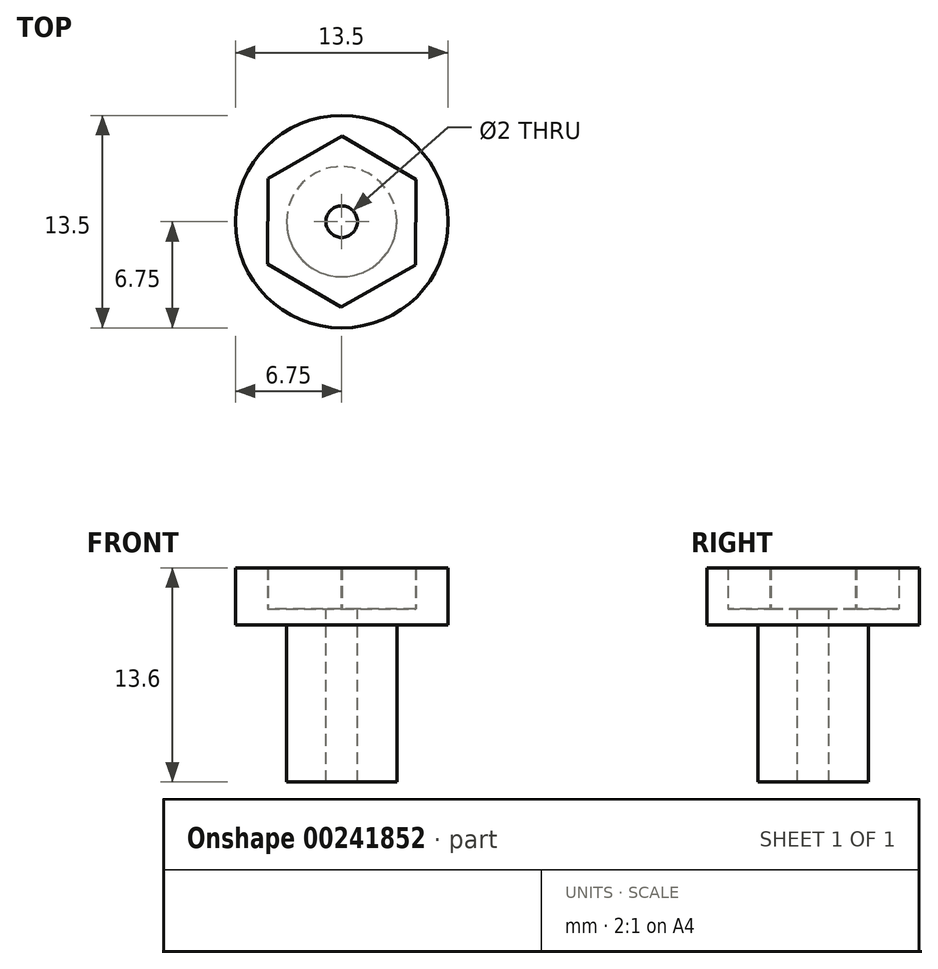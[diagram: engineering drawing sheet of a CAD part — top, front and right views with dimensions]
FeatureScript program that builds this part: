
annotation { "Feature Type Name" : "Feature", "Feature Type Description" : "" }
export const myFeature = defineFeature(function(context is Context, id is Id, definition is map)
    precondition{}
    {
        {
            var Q0;
            Q0=qCreatedBy(makeId("Top.planeOp"),FACE);
            var sketch = newSketch(context, id + "F0", { "sketchPlane" : qUnion([Q0])});
            skCircle(sketch, "E0", {"center": v(0, 0) * mm, "radius": 6.75 * mm});
            skCircle(sketch, "E1.cCircle", {"center": v(0, 0) * mm, "radius": 4.7 * mm, "construction": true});
            skLineSegment(sketch, "E1.0", {"start": v(0.04, 5.43) * mm, "end": v(4.72, 2.68) * mm});
            skLineSegment(sketch, "E1.1", {"start": v(4.72, 2.68) * mm, "end": v(4.68, -2.75) * mm});
            skLineSegment(sketch, "E1.2", {"start": v(4.68, -2.75) * mm, "end": v(-0.04, -5.43) * mm});
            skLineSegment(sketch, "E1.3", {"start": v(-0.04, -5.43) * mm, "end": v(-4.72, -2.68) * mm});
            skLineSegment(sketch, "E1.4", {"start": v(-4.72, -2.68) * mm, "end": v(-4.68, 2.75) * mm});
            skLineSegment(sketch, "E1.5", {"start": v(-4.68, 2.75) * mm, "end": v(0.04, 5.43) * mm});
            skPoint(sketch, "E1.0.midPoint", {"position": v(2.38, 4.05) * mm});
            skSolve(sketch);
        }
        {
            var Q0;
            Q0=qSketchRegion(id+"F0",true);
            extrude(context, id + "F1", {"entities" : qUnion([Q0]), "depth" : 3.6 * mm});
        }
        {
            var Q0;
            Q0=makeQuery(id+"F0.imprint","IMPRINT",FACE,{"disambiguationData":[TD([[makeQuery(id+"F0.imprint","IMPRINT",EDGE,{"derivedFrom":sQuery(id+"F0.wireOp",EDGE,"E1.0")}),-1.0]])]});
            extrude(context, id + "F2", {"entities" : qUnion([Q0]), "operationType" : NewBodyOperationType.ADD, "depth" : 1 * mm});
        }
        {
            var Q0;
            Q0=makeQuery(id+"F2.opExtrude","CAP_FACE",FACE,{"disambiguationData":[OSD([sQuery(id+"F0.wireOp",EDGE,"E1.0"),sQuery(id+"F0.wireOp",EDGE,"E1.1"),sQuery(id+"F0.wireOp",EDGE,"E1.2"),sQuery(id+"F0.wireOp",EDGE,"E1.3"),sQuery(id+"F0.wireOp",EDGE,"E1.4"),sQuery(id+"F0.wireOp",EDGE,"E1.5")])],"isStart":false});
            var sketch = newSketch(context, id + "F3", { "sketchPlane" : qUnion([Q0])});
            skCircle(sketch, "E2", {"center": v(0, 0) * mm, "radius": 1 * mm});
            skSolve(sketch);
        }
        {
            var Q0;
            Q0=qSketchRegion(id+"F3",true);
            extrude(context, id + "F4", {"entities" : qUnion([Q0]), "operationType" : NewBodyOperationType.REMOVE, "oppositeDirection" : true, "depth" : 25 * mm});
        }
        {
            var Q0;
            Q0=makeQuery(id+"F0.imprint","IMPRINT",FACE,{"disambiguationData":[TD([[makeQuery(id+"F0.imprint","IMPRINT",EDGE,{"derivedFrom":sQuery(id+"F0.wireOp",EDGE,"E0")}),1.0]])]});
            var sketch = newSketch(context, id + "F5", { "sketchPlane" : qUnion([Q0])});
            skCircle(sketch, "E3", {"center": v(0, 0) * mm, "radius": 3.5 * mm});
            skLineSegment(sketch, "E4", {"start": v(0, 0) * mm, "end": v(0, -2.6) * mm, "construction": true});
            skFitSpline(sketch, "E5", {"points": [v(-0.3, -0.95) * mm, v(0, -2.6) * mm, v(0.3, -0.95) * mm], "startDerivative": vector(0.26, -4.97) * mm, "endDerivative": vector(0.25, 4.96) * mm});
            skArc(sketch, "E6", {"start": v(-0.3, -0.95) * mm, "mid": v(0, -1) * mm, "end": v(0.3, -0.95) * mm});
            skSolve(sketch);
        }
        {
            var Q0;
            Q0=makeQuery(id+"F5.imprint","IMPRINT",FACE,{"disambiguationData":[TD([[makeQuery(id+"F5.imprint","IMPRINT",EDGE,{"derivedFrom":sQuery(id+"F5.wireOp",EDGE,"E5")}),1.0]])]});
            var Q1;
            Q1=sQuery(id+"F5.wireOp",EDGE,"E5");
            var Q2;
            Q2=sQuery(id+"F5.wireOp",EDGE,"E6");
            extrude(context, id + "F6", {"entities" : qUnion([Q0]), "operationType" : NewBodyOperationType.ADD, "surfaceEntities" : qUnion([Q1, Q2]), "oppositeDirection" : true, "depth" : 10 * mm});
        }
        {
            var Q0;
            Q0=qCreatedBy(makeId("Right.planeOp"),FACE);
            var sketch = newSketch(context, id + "F7", { "sketchPlane" : qUnion([Q0])});
            skLineSegment(sketch, "E7", {"start": v(0, 0) * mm, "end": v(0, 2.06) * mm, "construction": true});
            skSolve(sketch);
        }
        {
            var Q0;
            {var subQ0=sQuery(id+"F0.wireOp",EDGE,"E1.5");var subQ1=sQuery(id+"F0.wireOp",EDGE,"E1.4");var subQ2=sQuery(id+"F0.wireOp",EDGE,"E1.3");var subQ3=sQuery(id+"F0.wireOp",EDGE,"E1.2");var subQ4=sQuery(id+"F0.wireOp",EDGE,"E1.1");var subQ5=sQuery(id+"F0.wireOp",EDGE,"E1.0");Q0=makeQuery(id+"F2.boolean.opBoolean","MERGE",FACE,{"derivedFrom":[makeQuery(id+"F1.opExtrude","CAP_FACE",FACE,{"disambiguationData":[OSD([sQuery(id+"F0.wireOp",EDGE,"E0"),subQ5,subQ4,subQ3,subQ2,subQ1,subQ0])],"isStart":true}),makeQuery(id+"F2.opExtrude","CAP_FACE",FACE,{"disambiguationData":[OSD([subQ5,subQ4,subQ3,subQ2,subQ1,subQ0])],"isStart":true})]});}
            var sketch = newSketch(context, id + "F8", { "sketchPlane" : qUnion([Q0])});
            skCircle(sketch, "E8", {"center": v(0, 0) * mm, "radius": 3.5 * mm});
            skSolve(sketch);
        }
        {
            var Q0;
            Q0=makeQuery(id+"F8.imprint","IMPRINT",FACE,{"disambiguationData":[TD([[makeQuery(id+"F8.imprint","IMPRINT",EDGE,{"derivedFrom":sQuery(id+"F8.wireOp",EDGE,"E8")}),1.0]])]});
            extrude(context, id + "F9", {"entities" : qUnion([Q0]), "operationType" : NewBodyOperationType.ADD, "depth" : 10 * mm});
        }
    });
